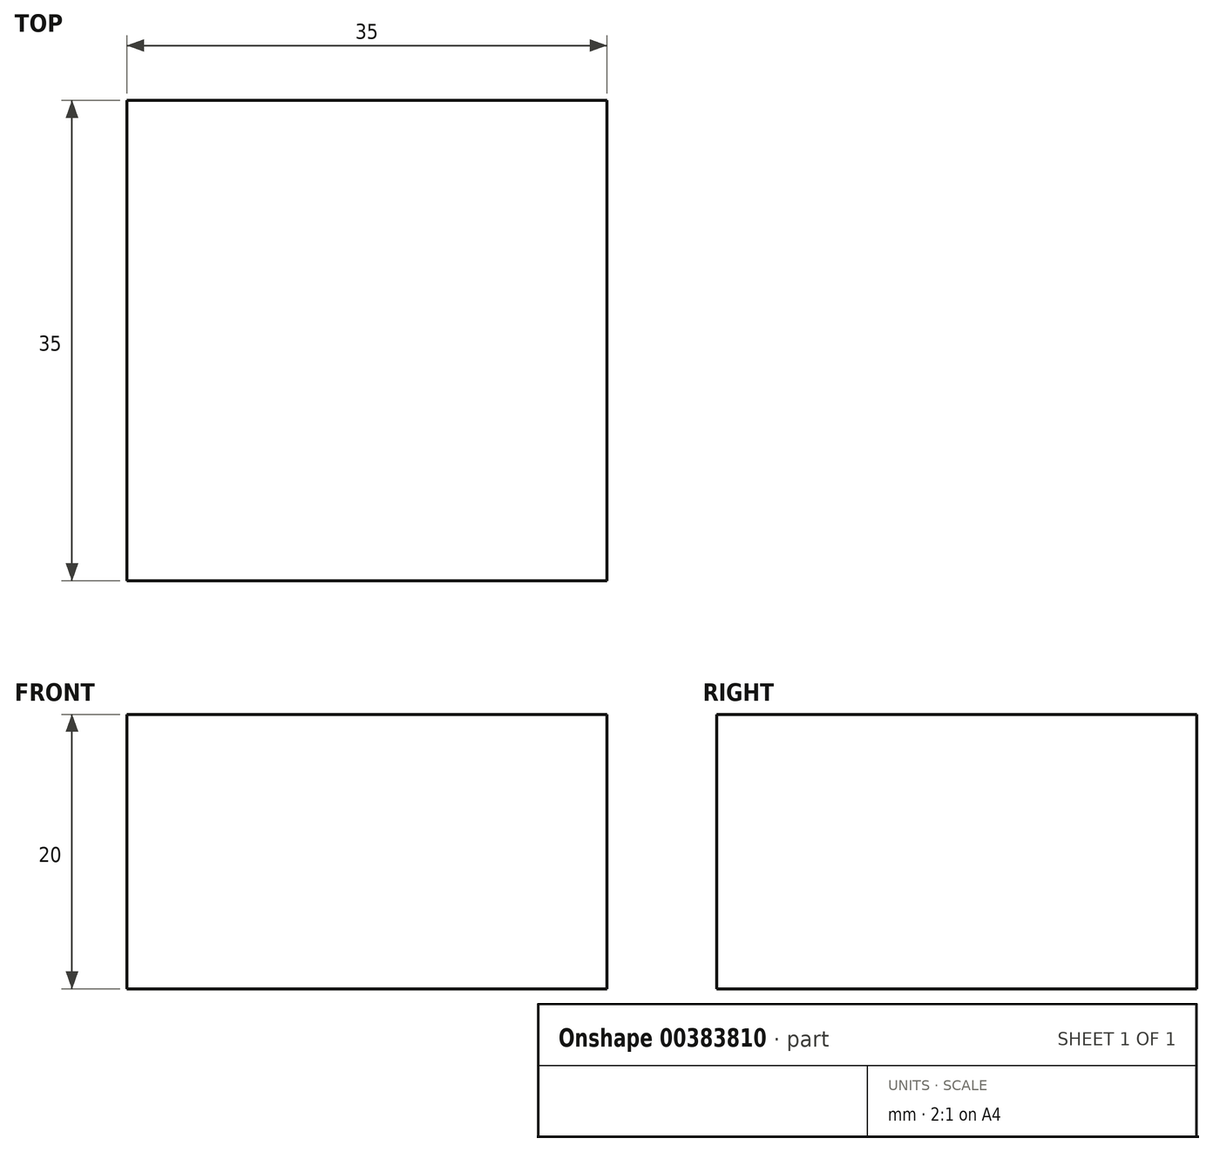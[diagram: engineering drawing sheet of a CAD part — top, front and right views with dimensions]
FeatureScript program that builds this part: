
annotation { "Feature Type Name" : "Feature", "Feature Type Description" : "" }
export const myFeature = defineFeature(function(context is Context, id is Id, definition is map)
    precondition{}
    {
        {
            var Q0;
            Q0=qCreatedBy(makeId("Top.planeOp"),FACE);
            var sketch = newSketch(context, id + "F0", { "sketchPlane" : qUnion([Q0])});
            skLineSegment(sketch, "E0.bottom", {"start": v(17.5, 17.5) * mm, "end": v(-17.5, 17.5) * mm});
            skLineSegment(sketch, "E0.top", {"start": v(17.5, -17.5) * mm, "end": v(-17.5, -17.5) * mm});
            skLineSegment(sketch, "E0.left", {"start": v(17.5, 17.5) * mm, "end": v(17.5, -17.5) * mm});
            skLineSegment(sketch, "E0.right", {"start": v(-17.5, 17.5) * mm, "end": v(-17.5, -17.5) * mm});
            skPoint(sketch, "E0.middle", {"position": v(0, 0) * mm});
            skSolve(sketch);
        }
        {
            var Q0;
            Q0 = qSketchRegion(id + "F0", true);
            extrude(context, id + "F1", {"entities" : qUnion([Q0]), "depth" : 20 * mm});
        }
    });
